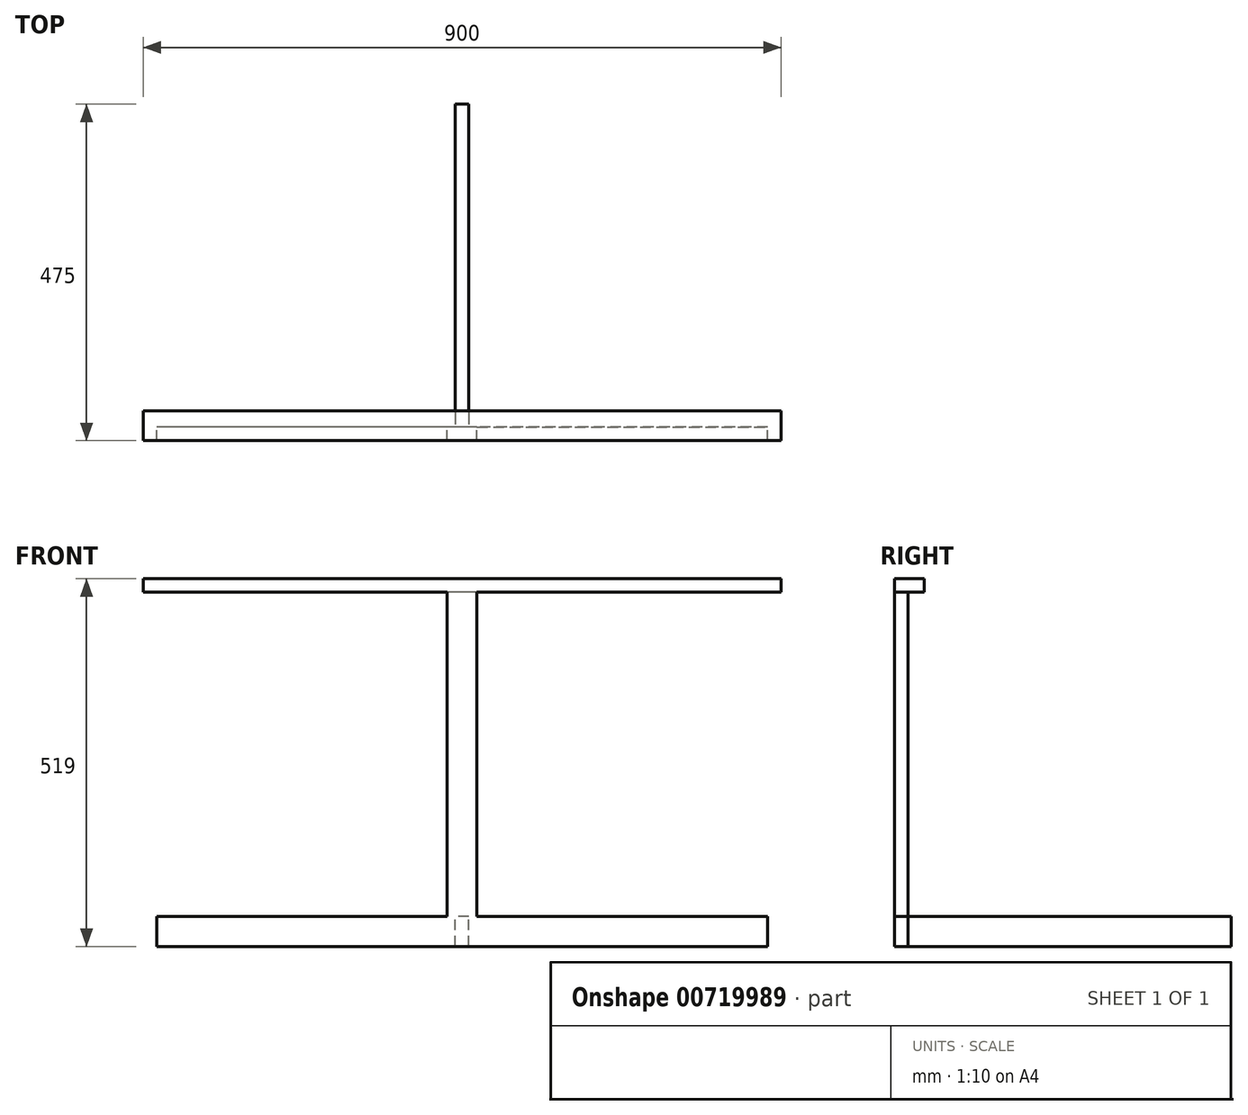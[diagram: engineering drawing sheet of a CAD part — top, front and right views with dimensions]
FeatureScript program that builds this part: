
annotation { "Feature Type Name" : "Feature", "Feature Type Description" : "" }
export const myFeature = defineFeature(function(context is Context, id is Id, definition is map)
    precondition{}
    {
        {
            var Q0;
            Q0=qCreatedBy(makeId("Front.planeOp"),FACE);
            var sketch = newSketch(context, id + "F0", { "sketchPlane" : qUnion([Q0])});
            skLineSegment(sketch, "E0.bottom", {"start": v(21, -229) * mm, "end": v(-21, -229) * mm});
            skLineSegment(sketch, "E0.top", {"start": v(21, 229) * mm, "end": v(-21, 229) * mm});
            skLineSegment(sketch, "E0.left", {"start": v(21, -229) * mm, "end": v(21, 229) * mm});
            skLineSegment(sketch, "E0.right", {"start": v(-21, -229) * mm, "end": v(-21, 229) * mm});
            skPoint(sketch, "E0.middle", {"position": v(0, 0) * mm});
            skLineSegment(sketch, "E1.bottom", {"start": v(0, -229) * mm, "end": v(431, -229) * mm});
            skLineSegment(sketch, "E1.top", {"start": v(0, -271) * mm, "end": v(431, -271) * mm});
            skLineSegment(sketch, "E1.left", {"start": v(0, -229) * mm, "end": v(0, -271) * mm});
            skLineSegment(sketch, "E1.right", {"start": v(431, -229) * mm, "end": v(431, -271) * mm});
            skLineSegment(sketch, "E2.bottom", {"start": v(0, -229) * mm, "end": v(-431, -229) * mm});
            skLineSegment(sketch, "E2.top", {"start": v(0, -271) * mm, "end": v(-431, -271) * mm});
            skLineSegment(sketch, "E2.right", {"start": v(-431, -229) * mm, "end": v(-431, -271) * mm});
            skLineSegment(sketch, "E3.bottom", {"start": v(9.5, -271) * mm, "end": v(-9.5, -271) * mm});
            skLineSegment(sketch, "E3.top", {"start": v(9.5, -229) * mm, "end": v(-9.5, -229) * mm});
            skLineSegment(sketch, "E3.left", {"start": v(9.5, -271) * mm, "end": v(9.5, -229) * mm});
            skLineSegment(sketch, "E3.right", {"start": v(-9.5, -271) * mm, "end": v(-9.5, -229) * mm});
            skPoint(sketch, "E3.middle", {"position": v(0, -250) * mm});
            skLineSegment(sketch, "E4.bottom", {"start": v(0, 229) * mm, "end": v(450, 229) * mm});
            skLineSegment(sketch, "E4.top", {"start": v(0, 248) * mm, "end": v(450, 248) * mm});
            skLineSegment(sketch, "E4.left", {"start": v(0, 229) * mm, "end": v(0, 248) * mm});
            skLineSegment(sketch, "E4.right", {"start": v(450, 229) * mm, "end": v(450, 248) * mm});
            skLineSegment(sketch, "E5.bottom", {"start": v(0, 229) * mm, "end": v(-450, 229) * mm});
            skLineSegment(sketch, "E5.top", {"start": v(0, 248) * mm, "end": v(-450, 248) * mm});
            skLineSegment(sketch, "E5.right", {"start": v(-450, 229) * mm, "end": v(-450, 248) * mm});
            skSolve(sketch);
        }
        {
            var Q0;
            Q0 = qSketchRegion(id + "F0", true);
            extrude(context, id + "F1", {"entities" : qUnion([Q0]), "depth" : 19 * mm, "offsetDistance" : 25 * mm});
        }
        {
            var Q0;
            {var subQ0=sQuery(id+"F0.wireOp",EDGE,"E1.left");Q0=makeQuery(id+"F0.imprint","IMPRINT",FACE,{"disambiguationData":[TD([[makeQuery(id+"F0.imprint","IMPRINT",EDGE,{"derivedFrom":subQ0}),-1.0]])]});}
            var Q1;
            {var subQ0=sQuery(id+"F0.wireOp",EDGE,"E1.left");Q1=makeQuery(id+"F0.imprint","IMPRINT",FACE,{"disambiguationData":[TD([[makeQuery(id+"F0.imprint","IMPRINT",EDGE,{"derivedFrom":subQ0}),1.0]])]});}
            extrude(context, id + "F2", {"entities" : qUnion([Q0, Q1]), "operationType" : NewBodyOperationType.ADD, "oppositeDirection" : true, "depth" : 456 * mm, "offsetDistance" : 25 * mm});
        }
        {
            var Q0;
            Q0=makeQuery(id+"F0.imprint","IMPRINT",FACE,{"disambiguationData":[TD([[makeQuery(id+"F0.imprint","IMPRINT",EDGE,{"derivedFrom":sQuery(id+"F0.wireOp",EDGE,"E4.top")}),-1.0]])]});
            var Q1;
            Q1=makeQuery(id+"F0.imprint","IMPRINT",FACE,{"disambiguationData":[TD([[makeQuery(id+"F0.imprint","IMPRINT",EDGE,{"derivedFrom":sQuery(id+"F0.wireOp",EDGE,"E5.top")}),1.0]])]});
            extrude(context, id + "F3", {"entities" : qUnion([Q0, Q1]), "operationType" : NewBodyOperationType.ADD, "oppositeDirection" : true, "depth" : 23 * mm, "offsetDistance" : 25 * mm});
        }
    });
